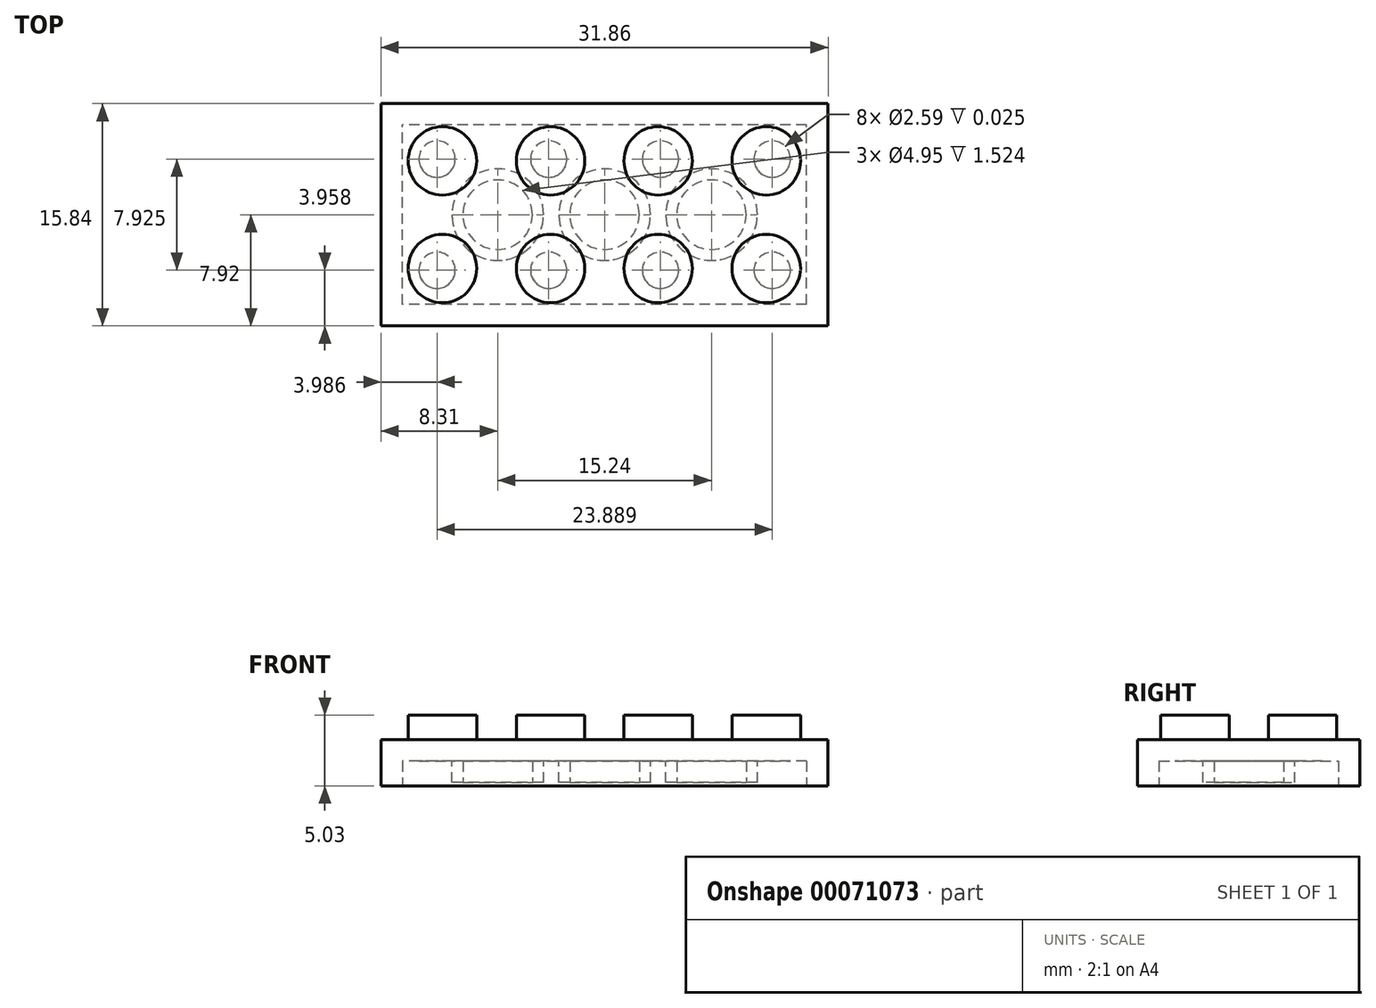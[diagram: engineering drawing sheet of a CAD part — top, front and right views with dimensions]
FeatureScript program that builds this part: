
annotation { "Feature Type Name" : "Feature", "Feature Type Description" : "" }
export const myFeature = defineFeature(function(context is Context, id is Id, definition is map)
    precondition{}
    {
        {
            var Q0;
            Q0=qCreatedBy(makeId("Top.planeOp"),FACE);
            var sketch = newSketch(context, id + "F0", { "sketchPlane" : qUnion([Q0])});
            skLineSegment(sketch, "E0.rect.bottom", {"start": v(15.93, -7.92) * mm, "end": v(-15.93, -7.92) * mm});
            skLineSegment(sketch, "E0.rect.top", {"start": v(15.93, 7.92) * mm, "end": v(-15.93, 7.92) * mm});
            skLineSegment(sketch, "E0.rect.left", {"start": v(15.93, -7.92) * mm, "end": v(15.93, 7.92) * mm});
            skLineSegment(sketch, "E0.rect.right", {"start": v(-15.93, -7.92) * mm, "end": v(-15.93, 7.92) * mm});
            skPoint(sketch, "E0.rect.middle", {"position": v(0, 0) * mm});
            skSolve(sketch);
        }
        {
            var Q0;
            Q0 = qSketchRegion(id + "F0", true);
            extrude(context, id + "F1", {"entities" : qUnion([Q0]), "depth" : 3.28 * mm});
        }
        {
            var Q0;
            Q0=makeQuery(id+"F1.opExtrude","CAP_FACE",FACE,{"disambiguationData":[OSD([sQuery(id+"F0.wireOp",EDGE,"E0.rect.bottom"),sQuery(id+"F0.wireOp",EDGE,"E0.rect.top"),sQuery(id+"F0.wireOp",EDGE,"E0.rect.left"),sQuery(id+"F0.wireOp",EDGE,"E0.rect.right")])],"isStart":true});
            shell(context, id + "F2", {"entities" : qUnion([Q0]), "thickness" : 1.52 * mm});
        }
        {
            var Q0;
            Q0=makeQuery(id+"F2.opShell","OFFSET_FACE",FACE,{"disambiguationData":[OSD([sQuery(id+"F0.wireOp",EDGE,"E0.rect.bottom"),sQuery(id+"F0.wireOp",EDGE,"E0.rect.top"),sQuery(id+"F0.wireOp",EDGE,"E0.rect.left"),sQuery(id+"F0.wireOp",EDGE,"E0.rect.right")])]});
            var sketch = newSketch(context, id + "F3", { "sketchPlane" : qUnion([Q0])});
            skCircle(sketch, "E1", {"center": v(0, 0) * mm, "radius": 3.26 * mm});
            skCircle(sketch, "E2", {"center": v(-7.62, 0) * mm, "radius": 3.26 * mm});
            skCircle(sketch, "E3", {"center": v(7.62, 0) * mm, "radius": 3.26 * mm});
            skSolve(sketch);
        }
        {
            var Q0;
            Q0 = qSketchRegion(id + "F3", true);
            extrude(context, id + "F4", {"entities" : qUnion([Q0]), "operationType" : NewBodyOperationType.ADD, "depth" : 1.52 * mm});
        }
        {
            var Q0;
            Q0=makeQuery(id+"F4.opExtrude","CAP_FACE",FACE,{"disambiguationData":[OSD([sQuery(id+"F3.wireOp",EDGE,"E1")])],"isStart":false});
            var sketch = newSketch(context, id + "F5", { "sketchPlane" : qUnion([Q0])});
            skCircle(sketch, "E4", {"center": v(0, 0) * mm, "radius": 2.48 * mm});
            skSolve(sketch);
        }
        {
            var Q0;
            Q0=makeQuery(id+"F4.opExtrude","CAP_FACE",FACE,{"disambiguationData":[OSD([sQuery(id+"F3.wireOp",EDGE,"E2")])],"isStart":false});
            var sketch = newSketch(context, id + "F6", { "sketchPlane" : qUnion([Q0])});
            skCircle(sketch, "E5", {"center": v(-7.62, 0) * mm, "radius": 2.48 * mm});
            skSolve(sketch);
        }
        {
            var Q0;
            Q0=makeQuery(id+"F4.opExtrude","CAP_FACE",FACE,{"disambiguationData":[OSD([sQuery(id+"F3.wireOp",EDGE,"E3")])],"isStart":false});
            var sketch = newSketch(context, id + "F7", { "sketchPlane" : qUnion([Q0])});
            skCircle(sketch, "E6", {"center": v(7.62, 0) * mm, "radius": 2.48 * mm});
            skSolve(sketch);
        }
        {
            var Q0;
            Q0 = qSketchRegion(id + "F5", true);
            extrude(context, id + "F8", {"entities" : qUnion([Q0]), "operationType" : NewBodyOperationType.REMOVE, "oppositeDirection" : true, "depth" : 1.52 * mm});
        }
        {
            var Q0;
            Q0 = qSketchRegion(id + "F6", true);
            extrude(context, id + "F9", {"entities" : qUnion([Q0]), "operationType" : NewBodyOperationType.REMOVE, "oppositeDirection" : true, "depth" : 1.52 * mm});
        }
        {
            var Q0;
            Q0 = qSketchRegion(id + "F7", true);
            extrude(context, id + "F10", {"entities" : qUnion([Q0]), "operationType" : NewBodyOperationType.REMOVE, "oppositeDirection" : true, "depth" : 1.52 * mm});
        }
        {
            var Q0;
            Q0=makeQuery(id+"F1.opExtrude","CAP_FACE",FACE,{"disambiguationData":[OSD([sQuery(id+"F0.wireOp",EDGE,"E0.rect.bottom"),sQuery(id+"F0.wireOp",EDGE,"E0.rect.top"),sQuery(id+"F0.wireOp",EDGE,"E0.rect.left"),sQuery(id+"F0.wireOp",EDGE,"E0.rect.right")])],"isStart":false});
            var sketch = newSketch(context, id + "F11", { "sketchPlane" : qUnion([Q0])});
            skCircle(sketch, "E7", {"center": v(-11.56, 3.84) * mm, "radius": 2.44 * mm});
            skCircle(sketch, "E8", {"center": v(-3.85, 3.84) * mm, "radius": 2.44 * mm});
            skCircle(sketch, "E9", {"center": v(3.82, 3.84) * mm, "radius": 2.44 * mm});
            skCircle(sketch, "E10", {"center": v(11.52, 3.84) * mm, "radius": 2.44 * mm});
            skCircle(sketch, "E11", {"center": v(11.52, -3.83) * mm, "radius": 2.44 * mm});
            skCircle(sketch, "E12", {"center": v(3.82, -3.83) * mm, "radius": 2.44 * mm});
            skCircle(sketch, "E13", {"center": v(-3.85, -3.83) * mm, "radius": 2.44 * mm});
            skCircle(sketch, "E14", {"center": v(-11.56, -3.83) * mm, "radius": 2.44 * mm});
            skSolve(sketch);
        }
        {
            var Q0;
            Q0 = qSketchRegion(id + "F11", true);
            extrude(context, id + "F12", {"entities" : qUnion([Q0]), "operationType" : NewBodyOperationType.ADD, "depth" : 1.75 * mm});
        }
        {
            var Q0;
            Q0=makeQuery(id+"F1.opExtrude","CAP_FACE",FACE,{"disambiguationData":[OSD([sQuery(id+"F0.wireOp",EDGE,"E0.rect.bottom"),sQuery(id+"F0.wireOp",EDGE,"E0.rect.top"),sQuery(id+"F0.wireOp",EDGE,"E0.rect.left"),sQuery(id+"F0.wireOp",EDGE,"E0.rect.right")])],"isStart":true});
            var sketch = newSketch(context, id + "F13", { "sketchPlane" : qUnion([Q0])});
            skCircle(sketch, "E15", {"center": v(-3.98, 3.96) * mm, "radius": 1.3 * mm});
            skCircle(sketch, "E16", {"center": v(-11.94, 3.96) * mm, "radius": 1.3 * mm});
            skCircle(sketch, "E17", {"center": v(-11.94, -3.96) * mm, "radius": 1.3 * mm});
            skCircle(sketch, "E18", {"center": v(-3.98, -3.96) * mm, "radius": 1.3 * mm});
            skCircle(sketch, "E19", {"center": v(3.98, -3.96) * mm, "radius": 1.3 * mm});
            skCircle(sketch, "E20", {"center": v(11.94, -3.96) * mm, "radius": 1.3 * mm});
            skCircle(sketch, "E21", {"center": v(11.94, 3.96) * mm, "radius": 1.3 * mm});
            skCircle(sketch, "E22", {"center": v(3.98, 3.96) * mm, "radius": 1.3 * mm});
            skSolve(sketch);
        }
        {
            var Q0;
            Q0 = qSketchRegion(id + "F13", true);
            extrude(context, id + "F14", {"entities" : qUnion([Q0]), "operationType" : NewBodyOperationType.REMOVE, "oppositeDirection" : true, "depth" : 1.78 * mm});
        }
    });
